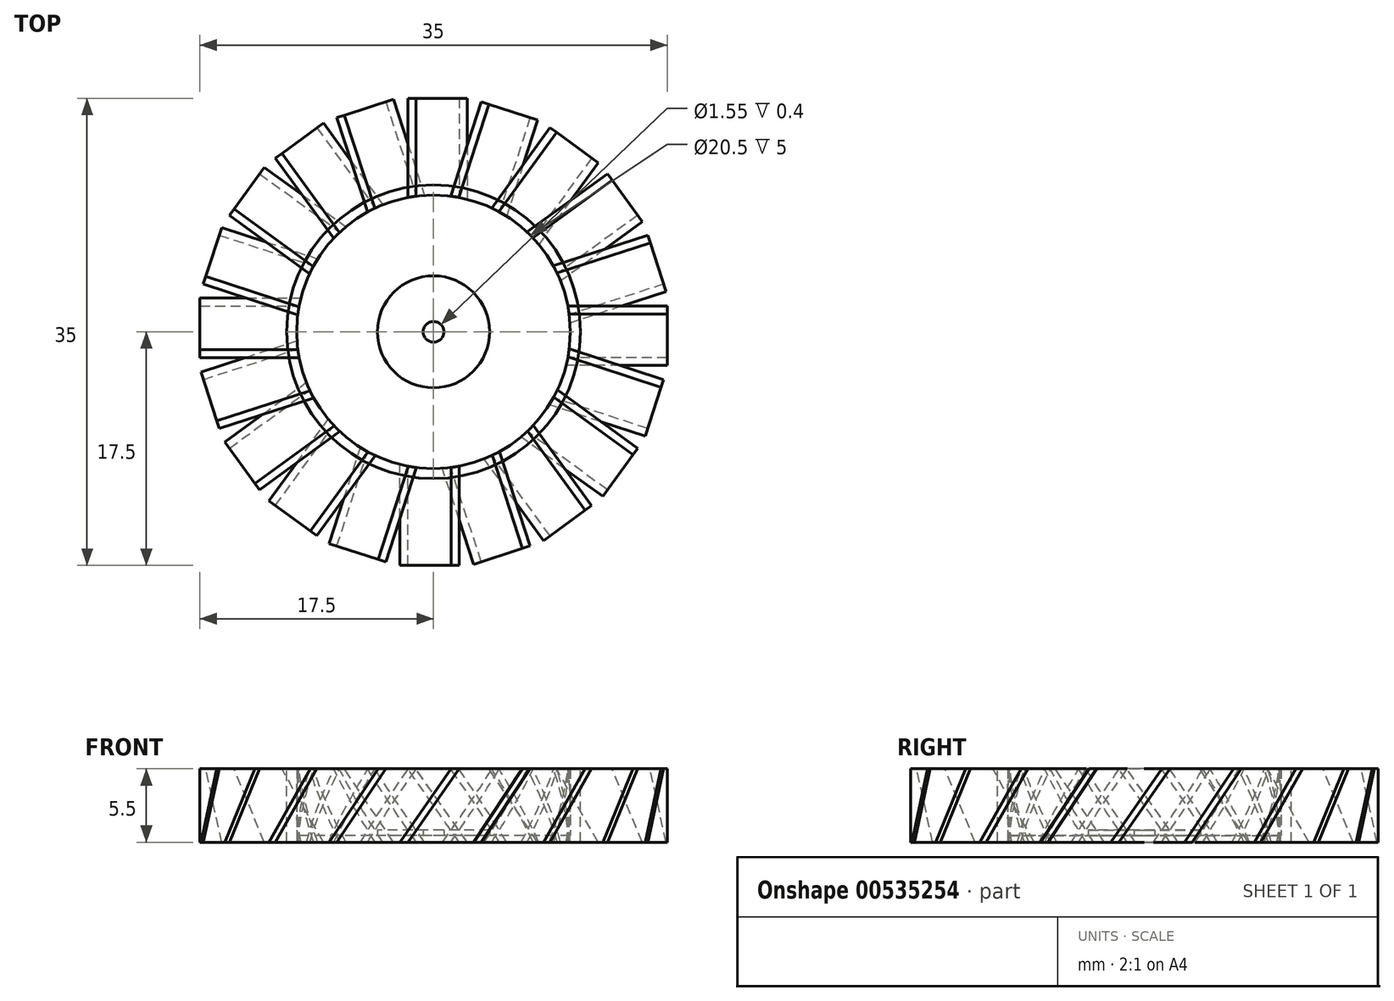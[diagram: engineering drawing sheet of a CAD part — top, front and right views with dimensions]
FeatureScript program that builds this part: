
annotation { "Feature Type Name" : "Feature", "Feature Type Description" : "" }
export const myFeature = defineFeature(function(context is Context, id is Id, definition is map)
    precondition{}
    {
        {
            var Q0;
            Q0=qCreatedBy(makeId("Top.planeOp"),FACE);
            var sketch = newSketch(context, id + "F0", { "sketchPlane" : qUnion([Q0])});
            skCircle(sketch, "E0", {"center": v(0, 0) * mm, "radius": 0.78 * mm});
            skCircle(sketch, "E1", {"center": v(0, 0) * mm, "radius": 4.2 * mm});
            skCircle(sketch, "E2", {"center": v(0, 0) * mm, "radius": 9 * mm});
            skCircle(sketch, "E3", {"center": v(0, 0) * mm, "radius": 11 * mm});
            skCircle(sketch, "E4", {"center": v(0, 0) * mm, "radius": 10.25 * mm});
            skSolve(sketch);
        }
        {
            var Q0;
            Q0=makeQuery(id+"F0.imprint","IMPRINT",FACE,{"disambiguationData":[TD([[makeQuery(id+"F0.imprint","IMPRINT",EDGE,{"derivedFrom":sQuery(id+"F0.wireOp",EDGE,"E3")}),1.0]])]});
            var Q1;
            Q1=makeQuery(id+"F0.imprint","IMPRINT",FACE,{"disambiguationData":[TD([[makeQuery(id+"F0.imprint","IMPRINT",EDGE,{"derivedFrom":sQuery(id+"F0.wireOp",EDGE,"E0")}),-1.0]])]});
            var Q2;
            Q2=makeQuery(id+"F0.imprint","IMPRINT",FACE,{"disambiguationData":[TD([[makeQuery(id+"F0.imprint","IMPRINT",EDGE,{"derivedFrom":sQuery(id+"F0.wireOp",EDGE,"E1")}),-1.0]])]});
            var Q3;
            Q3=makeQuery(id+"F0.imprint","IMPRINT",FACE,{"disambiguationData":[TD([[makeQuery(id+"F0.imprint","IMPRINT",EDGE,{"derivedFrom":sQuery(id+"F0.wireOp",EDGE,"E2")}),-1.0]])]});
            var Q4;
            Q4=makeQuery(id+"F0.imprint","IMPRINT",FACE,{"disambiguationData":[TD([[makeQuery(id+"F0.imprint","IMPRINT",EDGE,{"derivedFrom":sQuery(id+"F0.wireOp",EDGE,"E0")}),1.0]])]});
            extrude(context, id + "F1", {"entities" : qUnion([Q0, Q1, Q2, Q3, Q4]), "oppositeDirection" : true, "depth" : .5 * mm});
        }
        {
            var Q0;
            Q0=makeQuery(id+"F0.imprint","IMPRINT",FACE,{"disambiguationData":[TD([[makeQuery(id+"F0.imprint","IMPRINT",EDGE,{"derivedFrom":sQuery(id+"F0.wireOp",EDGE,"E0")}),-1.0]])]});
            extrude(context, id + "F2", {"entities" : qUnion([Q0]), "operationType" : NewBodyOperationType.ADD, "depth" : .4 * mm});
        }
        {
            var Q0;
            Q0=makeQuery(id+"F0.imprint","IMPRINT",FACE,{"disambiguationData":[TD([[makeQuery(id+"F0.imprint","IMPRINT",EDGE,{"derivedFrom":sQuery(id+"F0.wireOp",EDGE,"E3")}),1.0]])]});
            extrude(context, id + "F3", {"entities" : qUnion([Q0]), "operationType" : NewBodyOperationType.ADD, "depth" : 5 * mm});
        }
        {
            var Q0;
            Q0=qCreatedBy(makeId("Front.planeOp"),FACE);
            var sketch = newSketch(context, id + "F4", { "sketchPlane" : qUnion([Q0])});
            skLineSegment(sketch, "E5.0", {"start": v(-11, 5) * mm, "end": v(11, 5) * mm});
            skLineSegment(sketch, "E5.1", {"start": v(-11, -0.5) * mm, "end": v(11, -0.5) * mm});
            skLineSegment(sketch, "E6", {"start": v(0, -0.5) * mm, "end": v(0, 5) * mm, "construction": true});
            skLineSegment(sketch, "E7", {"start": v(0, 2.25) * mm, "end": v(-1.93, 5) * mm});
            skLineSegment(sketch, "E8", {"start": v(0, 2.25) * mm, "end": v(1.93, -0.5) * mm});
            skLineSegment(sketch, "E9", {"start": v(2.53, -0.5) * mm, "end": v(-1.33, 5) * mm});
            skSolve(sketch);
        }
        {
            var Q0;
            {var subQ3=sQuery(id+"F4.wireOp",EDGE,"E7");Q0=makeQuery(id+"F4.imprint","IMPRINT",FACE,{"disambiguationData":[TD([[makeQuery(id+"F4.imprint","IMPRINT",EDGE,{"derivedFrom":subQ3}),-1.0]])]});}
            var Q1;
            Q1=makeQuery(id+"F3.opExtrude","SWEPT_FACE",FACE,{"disambiguationData":[OSD([sQuery(id+"F0.wireOp",EDGE,"E4")])]});
            var Q2;
            Q2=makeQuery(id+"F3.opExtrude","SWEPT_FACE",FACE,{"disambiguationData":[OSD([sQuery(id+"F0.wireOp",EDGE,"E4")])]});
            extrude(context, id + "F5", {"entities" : qUnion([Q0]), "oppositeDirection" : true, "endBoundEntityFace" : qUnion([Q1]), "depth" : 17.5 * mm, "hasSecondDirection" : true, "secondDirectionBound" : SecondDirectionBoundingType.UP_TO_SURFACE, "secondDirectionOppositeDirection" : true, "secondDirectionBoundEntityFace" : qUnion([Q2]), "secondDirectionDepth" : 25 * mm});
        }
        {
            var Q0;
            Q0=makeQuery(id+"F5.opExtrude","SWEPT_BODY",BODY,{"disambiguationData":[OSD([sQuery(id+"F4.wireOp",EDGE,"E5.0"),sQuery(id+"F4.wireOp",EDGE,"E5.1"),sQuery(id+"F4.wireOp",EDGE,"E7"),sQuery(id+"F4.wireOp",EDGE,"E8"),sQuery(id+"F4.wireOp",EDGE,"E9")])]});
            var Q1;
            {var subQ0=sQuery(id+"F0.wireOp",EDGE,"E3");Q1=makeQuery(id+"F3.boolean.opBoolean","MERGE",FACE,{"derivedFrom":[makeQuery(id+"F1.opExtrude","SWEPT_FACE",FACE,{"disambiguationData":[OSD([subQ0])]}),makeQuery(id+"F3.opExtrude","SWEPT_FACE",FACE,{"disambiguationData":[OSD([subQ0])]})]});}
            circularPattern(context, id + "F6", {"entities" : qUnion([Q0]), "axis" : qUnion([Q1]), "angle" : 18 * degree, "instanceCount" : 20});
        }
    });
